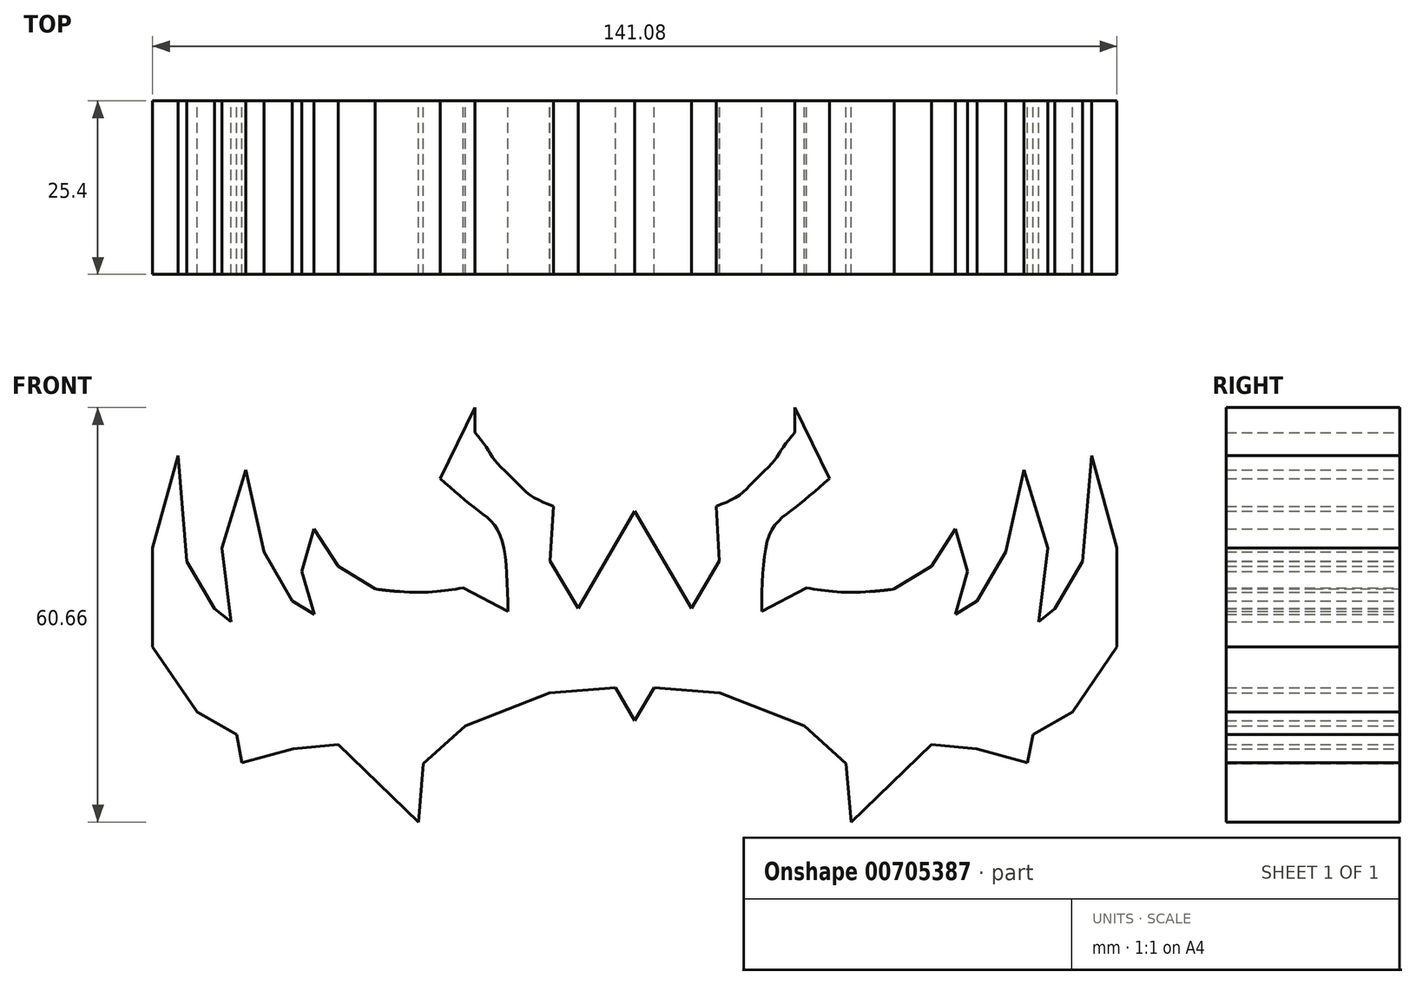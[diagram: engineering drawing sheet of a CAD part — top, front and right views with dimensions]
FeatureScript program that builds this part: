
annotation { "Feature Type Name" : "Feature", "Feature Type Description" : "" }
export const myFeature = defineFeature(function(context is Context, id is Id, definition is map)
    precondition{}
    {
        {
            var Q0;
            Q0=qCreatedBy(makeId("Front.planeOp"),FACE);
            var sketch = newSketch(context, id + "F0", { "sketchPlane" : qUnion([Q0])});
            skLineSegment(sketch, "E0", {"start": v(0, 0) * mm, "end": v(0, -3.04) * mm});
            skLineSegment(sketch, "E1", {"start": v(0, -3.04) * mm, "end": v(0, 0) * mm});
            skLineSegment(sketch, "E2", {"start": v(0, 15.49) * mm, "end": v(-8.28, 1.23) * mm});
            skLineSegment(sketch, "E3", {"start": v(-8.28, 1.23) * mm, "end": v(-12.37, 8.16) * mm});
            skLineSegment(sketch, "E4", {"start": v(-12.37, 8.16) * mm, "end": v(-11.9, 16.15) * mm});
            skFitSpline(sketch, "E5", {"points": [v(-11.9, 16.15) * mm, v(-15.37, 17.85) * mm, v(-17.68, 20.08) * mm, v(-20.4, 22.8) * mm, v(-21.58, 24.61) * mm, v(-23.4, 26.98) * mm], "startDerivative": vector(-17.13, 6.88) * mm, "endDerivative": vector(-10.36, 12.7) * mm});
            skLineSegment(sketch, "E6", {"start": v(-23.4, 26.98) * mm, "end": v(-23.4, 30.61) * mm});
            skLineSegment(sketch, "E7", {"start": v(-23.4, 30.61) * mm, "end": v(-28.49, 20.22) * mm});
            skFitSpline(sketch, "E8", {"points": [v(-28.49, 20.22) * mm, v(-23.37, 15.92) * mm, v(-19.88, 12.37) * mm, v(-18.57, 0.8) * mm], "startDerivative": vector(16.73, -14.68) * mm, "endDerivative": vector(0.35, -32.63) * mm});
            skLineSegment(sketch, "E9", {"start": v(-18.57, 0.8) * mm, "end": v(-25.11, 4.23) * mm});
            skFitSpline(sketch, "E10", {"points": [v(-25.11, 4.23) * mm, v(-32.14, 3.58) * mm, v(-37.97, 4.1) * mm, v(-37.97, 4.11) * mm, v(-37.98, 4.1) * mm], "startDerivative": vector(-12.52, -2.08) * mm, "endDerivative": vector(-0.69, -0.74) * mm});
            skLineSegment(sketch, "E11", {"start": v(-37.97, 4.11) * mm, "end": v(-43.4, 7.41) * mm});
            skLineSegment(sketch, "E12", {"start": v(-43.4, 7.41) * mm, "end": v(-46.92, 12.83) * mm});
            skLineSegment(sketch, "E13", {"start": v(-46.92, 12.83) * mm, "end": v(-48.7, 6.64) * mm});
            skLineSegment(sketch, "E14", {"start": v(-48.7, 6.64) * mm, "end": v(-46.89, 0.36) * mm});
            skLineSegment(sketch, "E15", {"start": v(-46.89, 0.36) * mm, "end": v(-50.1, 2.34) * mm});
            skLineSegment(sketch, "E16", {"start": v(-50.1, 2.34) * mm, "end": v(-54.25, 9.51) * mm});
            skLineSegment(sketch, "E17", {"start": v(-54.25, 9.51) * mm, "end": v(-56.92, 21.51) * mm});
            skLineSegment(sketch, "E18", {"start": v(-56.92, 21.51) * mm, "end": v(-60.41, 10.04) * mm});
            skLineSegment(sketch, "E19", {"start": v(-60.41, 10.04) * mm, "end": v(-59.08, -0.72) * mm});
            skLineSegment(sketch, "E20", {"start": v(-59.08, -0.72) * mm, "end": v(-61.47, 1.15) * mm});
            skLineSegment(sketch, "E21", {"start": v(-61.47, 1.15) * mm, "end": v(-65.53, 8.08) * mm});
            skLineSegment(sketch, "E22", {"start": v(-65.53, 8.08) * mm, "end": v(-66.84, 23.61) * mm});
            skLineSegment(sketch, "E23", {"start": v(-66.84, 23.61) * mm, "end": v(-70.54, 10.04) * mm});
            skLineSegment(sketch, "E24", {"start": v(-70.54, 10.04) * mm, "end": v(-70.54, -4.38) * mm});
            skLineSegment(sketch, "E25", {"start": v(-70.54, -4.38) * mm, "end": v(-64.04, -13.92) * mm});
            skLineSegment(sketch, "E26", {"start": v(-64.04, -13.92) * mm, "end": v(-58.26, -17.24) * mm});
            skLineSegment(sketch, "E27", {"start": v(-58.26, -17.24) * mm, "end": v(-57.47, -21.38) * mm});
            skLineSegment(sketch, "E28", {"start": v(-57.47, -21.38) * mm, "end": v(-50, -19.34) * mm});
            skLineSegment(sketch, "E29", {"start": v(-50, -19.34) * mm, "end": v(-43.4, -18.73) * mm});
            skLineSegment(sketch, "E30", {"start": v(-43.4, -18.73) * mm, "end": v(-31.64, -30.05) * mm});
            skLineSegment(sketch, "E31", {"start": v(-31.64, -30.05) * mm, "end": v(-30.93, -21.53) * mm});
            skLineSegment(sketch, "E32", {"start": v(-30.93, -21.53) * mm, "end": v(-24.8, -15.98) * mm});
            skLineSegment(sketch, "E33", {"start": v(-24.8, -15.98) * mm, "end": v(-12.45, -11.17) * mm});
            skLineSegment(sketch, "E34", {"start": v(-12.45, -11.17) * mm, "end": v(-2.8, -10.37) * mm});
            skLineSegment(sketch, "E35", {"start": v(-2.8, -10.37) * mm, "end": v(0, -15.23) * mm});
            skLineSegment(sketch, "E36", {"start": v(0, -15.23) * mm, "end": v(-2.8, -10.37) * mm});
            skLineSegment(sketch, "E37.MirrorCS", {"start": v(0, 15.49) * mm, "end": v(8.28, 1.23) * mm});
            skLineSegment(sketch, "E38.MirrorCS", {"start": v(0, -15.23) * mm, "end": v(2.8, -10.37) * mm});
            skLineSegment(sketch, "E39.MirrorCS", {"start": v(12.45, -11.17) * mm, "end": v(2.8, -10.37) * mm});
            skLineSegment(sketch, "E40.MirrorCS", {"start": v(8.28, 1.23) * mm, "end": v(12.37, 8.16) * mm});
            skLineSegment(sketch, "E41.MirrorCS", {"start": v(12.37, 8.16) * mm, "end": v(11.9, 16.15) * mm});
            skFitSpline(sketch, "E42.MirrorCS", {"points": [v(11.9, 16.15) * mm, v(15.37, 17.85) * mm, v(17.68, 20.08) * mm, v(20.4, 22.8) * mm, v(21.58, 24.61) * mm, v(23.4, 26.98) * mm], "startDerivative": vector(17.13, 6.88) * mm, "endDerivative": vector(10.36, 12.7) * mm});
            skLineSegment(sketch, "E43.MirrorCS", {"start": v(23.4, 30.61) * mm, "end": v(28.49, 20.22) * mm});
            skLineSegment(sketch, "E44.MirrorCS", {"start": v(23.4, 26.98) * mm, "end": v(23.4, 30.61) * mm});
            skFitSpline(sketch, "E45.MirrorCS", {"points": [v(28.49, 20.22) * mm, v(23.37, 15.92) * mm, v(19.88, 12.37) * mm, v(18.57, 0.8) * mm], "startDerivative": vector(-16.73, -14.68) * mm, "endDerivative": vector(-0.35, -32.63) * mm});
            skLineSegment(sketch, "E46.MirrorCS", {"start": v(18.57, 0.8) * mm, "end": v(25.11, 4.23) * mm});
            skFitSpline(sketch, "E47.MirrorCS", {"points": [v(25.11, 4.23) * mm, v(32.14, 3.58) * mm, v(37.97, 4.1) * mm, v(37.97, 4.11) * mm, v(37.98, 4.1) * mm], "startDerivative": vector(12.52, -2.08) * mm, "endDerivative": vector(0.69, -0.74) * mm});
            skLineSegment(sketch, "E48.MirrorCS", {"start": v(37.97, 4.11) * mm, "end": v(43.4, 7.41) * mm});
            skLineSegment(sketch, "E49.MirrorCS", {"start": v(43.4, 7.41) * mm, "end": v(46.92, 12.83) * mm});
            skLineSegment(sketch, "E50.MirrorCS", {"start": v(46.92, 12.83) * mm, "end": v(48.7, 6.64) * mm});
            skLineSegment(sketch, "E51.MirrorCS", {"start": v(48.7, 6.64) * mm, "end": v(46.89, 0.36) * mm});
            skLineSegment(sketch, "E52.MirrorCS", {"start": v(46.89, 0.36) * mm, "end": v(50.1, 2.34) * mm});
            skLineSegment(sketch, "E53.MirrorCS", {"start": v(50.1, 2.34) * mm, "end": v(54.25, 9.51) * mm});
            skLineSegment(sketch, "E54.MirrorCS", {"start": v(54.25, 9.51) * mm, "end": v(56.92, 21.51) * mm});
            skLineSegment(sketch, "E55.MirrorCS", {"start": v(56.92, 21.51) * mm, "end": v(60.41, 10.04) * mm});
            skLineSegment(sketch, "E56.MirrorCS", {"start": v(60.41, 10.04) * mm, "end": v(59.08, -0.72) * mm});
            skLineSegment(sketch, "E57.MirrorCS", {"start": v(59.08, -0.72) * mm, "end": v(61.47, 1.15) * mm});
            skLineSegment(sketch, "E58.MirrorCS", {"start": v(61.47, 1.15) * mm, "end": v(65.53, 8.08) * mm});
            skLineSegment(sketch, "E59.MirrorCS", {"start": v(65.53, 8.08) * mm, "end": v(66.84, 23.61) * mm});
            skLineSegment(sketch, "E60.MirrorCS", {"start": v(66.84, 23.61) * mm, "end": v(70.54, 10.04) * mm});
            skLineSegment(sketch, "E61.MirrorCS", {"start": v(70.54, 10.04) * mm, "end": v(70.54, -4.38) * mm});
            skLineSegment(sketch, "E62.MirrorCS", {"start": v(70.54, -4.38) * mm, "end": v(64.04, -13.92) * mm});
            skLineSegment(sketch, "E63.MirrorCS", {"start": v(64.04, -13.92) * mm, "end": v(58.26, -17.24) * mm});
            skLineSegment(sketch, "E64.MirrorCS", {"start": v(58.26, -17.24) * mm, "end": v(57.47, -21.38) * mm});
            skLineSegment(sketch, "E65.MirrorCS", {"start": v(57.47, -21.38) * mm, "end": v(50, -19.34) * mm});
            skLineSegment(sketch, "E66.MirrorCS", {"start": v(50, -19.34) * mm, "end": v(43.4, -18.73) * mm});
            skLineSegment(sketch, "E67.MirrorCS", {"start": v(43.4, -18.73) * mm, "end": v(31.64, -30.05) * mm});
            skLineSegment(sketch, "E68.MirrorCS", {"start": v(31.64, -30.05) * mm, "end": v(30.93, -21.53) * mm});
            skLineSegment(sketch, "E69.MirrorCS", {"start": v(30.93, -21.53) * mm, "end": v(24.8, -15.98) * mm});
            skLineSegment(sketch, "E70.MirrorCS", {"start": v(24.8, -15.98) * mm, "end": v(12.45, -11.17) * mm});
            skSolve(sketch);
        }
        {
            var Q0;
            Q0=makeQuery(id+"F0.imprint","IMPRINT",FACE,{"disambiguationData":[TD([[makeQuery(id+"F0.imprint","IMPRINT",EDGE,{"derivedFrom":sQuery(id+"F0.wireOp",EDGE,"E2")}),1.0]])]});
            extrude(context, id + "F1", {"entities" : qUnion([Q0]), "depth" : 12.7 * mm, "offsetDistance" : 25.4 * mm});
        }
        {
            var Q0;
            Q0=makeQuery(id+"F1.opExtrude","CAP_FACE",FACE,{"disambiguationData":[OSD([sQuery(id+"F0.wireOp",EDGE,"E2"),sQuery(id+"F0.wireOp",EDGE,"E3"),sQuery(id+"F0.wireOp",EDGE,"E4"),sQuery(id+"F0.wireOp",EDGE,"E5"),sQuery(id+"F0.wireOp",EDGE,"E6"),sQuery(id+"F0.wireOp",EDGE,"E7"),sQuery(id+"F0.wireOp",EDGE,"E8"),sQuery(id+"F0.wireOp",EDGE,"E9"),sQuery(id+"F0.wireOp",EDGE,"E10"),sQuery(id+"F0.wireOp",EDGE,"E11"),sQuery(id+"F0.wireOp",EDGE,"E12"),sQuery(id+"F0.wireOp",EDGE,"E13"),sQuery(id+"F0.wireOp",EDGE,"E14"),sQuery(id+"F0.wireOp",EDGE,"E15"),sQuery(id+"F0.wireOp",EDGE,"E16"),sQuery(id+"F0.wireOp",EDGE,"E17"),sQuery(id+"F0.wireOp",EDGE,"E18"),sQuery(id+"F0.wireOp",EDGE,"E19"),sQuery(id+"F0.wireOp",EDGE,"E20"),sQuery(id+"F0.wireOp",EDGE,"E21"),sQuery(id+"F0.wireOp",EDGE,"E22"),sQuery(id+"F0.wireOp",EDGE,"E23"),sQuery(id+"F0.wireOp",EDGE,"E24"),sQuery(id+"F0.wireOp",EDGE,"E25"),sQuery(id+"F0.wireOp",EDGE,"E26"),sQuery(id+"F0.wireOp",EDGE,"E27"),sQuery(id+"F0.wireOp",EDGE,"E28"),sQuery(id+"F0.wireOp",EDGE,"E29"),sQuery(id+"F0.wireOp",EDGE,"E30"),sQuery(id+"F0.wireOp",EDGE,"E31"),sQuery(id+"F0.wireOp",EDGE,"E32"),sQuery(id+"F0.wireOp",EDGE,"E33"),sQuery(id+"F0.wireOp",EDGE,"E34"),sQuery(id+"F0.wireOp",EDGE,"E36"),sQuery(id+"F0.wireOp",EDGE,"E37.MirrorCS"),sQuery(id+"F0.wireOp",EDGE,"E38.MirrorCS"),sQuery(id+"F0.wireOp",EDGE,"E39.MirrorCS"),sQuery(id+"F0.wireOp",EDGE,"E40.MirrorCS"),sQuery(id+"F0.wireOp",EDGE,"E41.MirrorCS"),sQuery(id+"F0.wireOp",EDGE,"E42.MirrorCS"),sQuery(id+"F0.wireOp",EDGE,"E43.MirrorCS"),sQuery(id+"F0.wireOp",EDGE,"E44.MirrorCS"),sQuery(id+"F0.wireOp",EDGE,"E45.MirrorCS"),sQuery(id+"F0.wireOp",EDGE,"E46.MirrorCS"),sQuery(id+"F0.wireOp",EDGE,"E47.MirrorCS"),sQuery(id+"F0.wireOp",EDGE,"E48.MirrorCS"),sQuery(id+"F0.wireOp",EDGE,"E49.MirrorCS"),sQuery(id+"F0.wireOp",EDGE,"E50.MirrorCS"),sQuery(id+"F0.wireOp",EDGE,"E51.MirrorCS"),sQuery(id+"F0.wireOp",EDGE,"E52.MirrorCS"),sQuery(id+"F0.wireOp",EDGE,"E53.MirrorCS"),sQuery(id+"F0.wireOp",EDGE,"E54.MirrorCS"),sQuery(id+"F0.wireOp",EDGE,"E55.MirrorCS"),sQuery(id+"F0.wireOp",EDGE,"E56.MirrorCS"),sQuery(id+"F0.wireOp",EDGE,"E57.MirrorCS"),sQuery(id+"F0.wireOp",EDGE,"E58.MirrorCS"),sQuery(id+"F0.wireOp",EDGE,"E59.MirrorCS"),sQuery(id+"F0.wireOp",EDGE,"E60.MirrorCS"),sQuery(id+"F0.wireOp",EDGE,"E61.MirrorCS"),sQuery(id+"F0.wireOp",EDGE,"E62.MirrorCS"),sQuery(id+"F0.wireOp",EDGE,"E63.MirrorCS"),sQuery(id+"F0.wireOp",EDGE,"E64.MirrorCS"),sQuery(id+"F0.wireOp",EDGE,"E65.MirrorCS"),sQuery(id+"F0.wireOp",EDGE,"E66.MirrorCS"),sQuery(id+"F0.wireOp",EDGE,"E67.MirrorCS"),sQuery(id+"F0.wireOp",EDGE,"E68.MirrorCS"),sQuery(id+"F0.wireOp",EDGE,"E69.MirrorCS"),sQuery(id+"F0.wireOp",EDGE,"E70.MirrorCS")])],"isStart":true});
            extrude(context, id + "F2", {"entities" : qUnion([Q0]), "operationType" : NewBodyOperationType.ADD, "depth" : 12.7 * mm, "offsetDistance" : 25.4 * mm});
        }
    });
